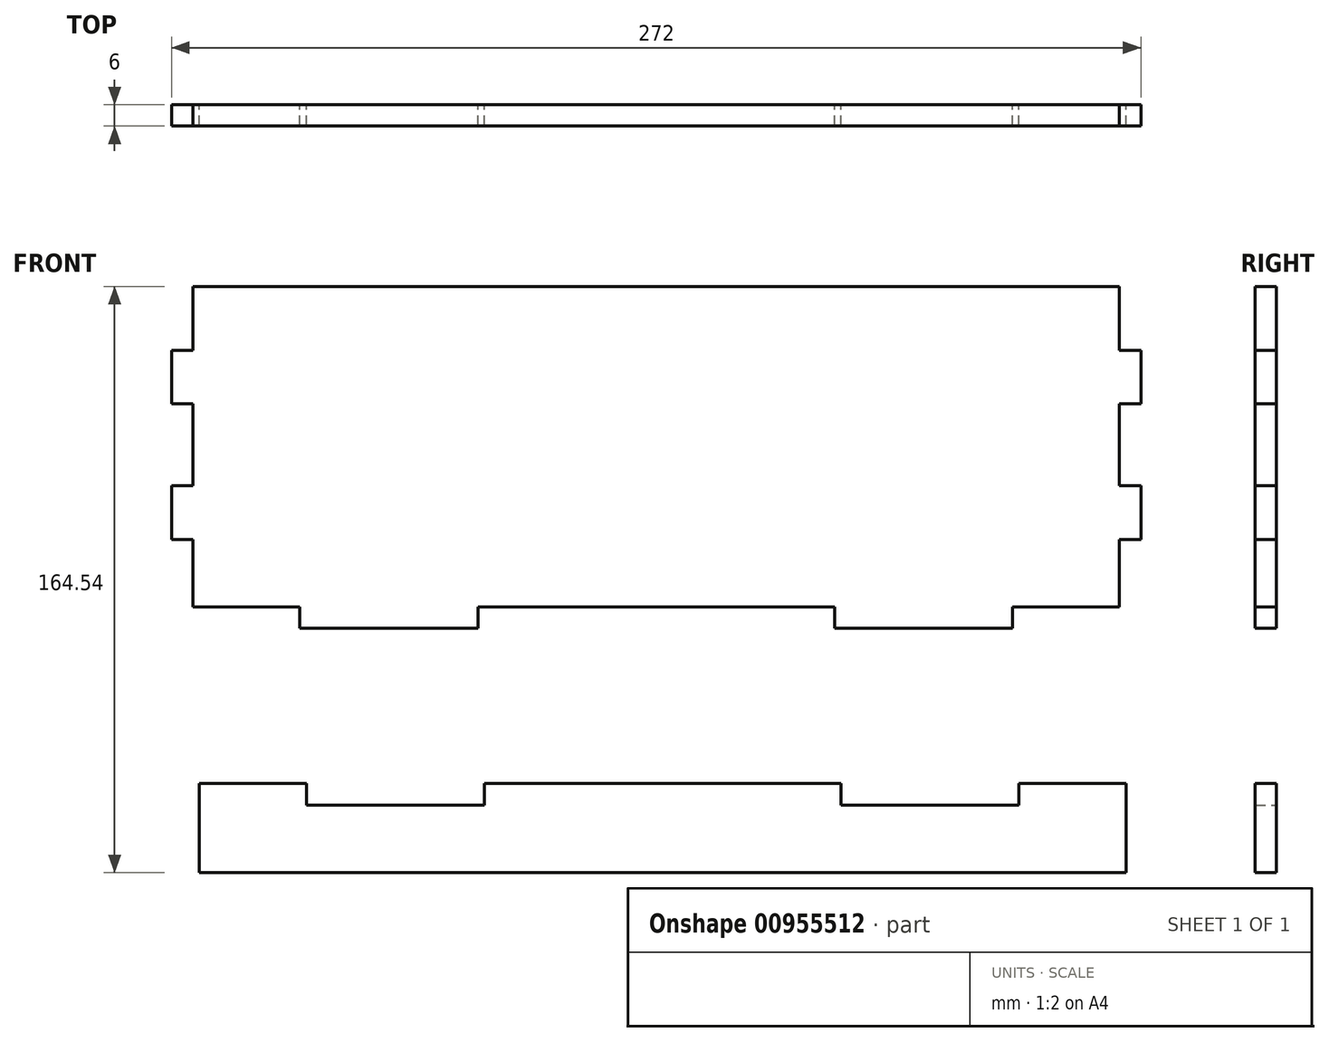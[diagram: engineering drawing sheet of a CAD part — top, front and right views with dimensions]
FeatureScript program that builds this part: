
annotation { "Feature Type Name" : "Feature", "Feature Type Description" : "" }
export const myFeature = defineFeature(function(context is Context, id is Id, definition is map)
    precondition{}
    {
        {
            var Q0;
            Q0=qCreatedBy(makeId("Front.planeOp"),FACE);
            var sketch = newSketch(context, id + "F0", { "sketchPlane" : qUnion([Q0])});
            skLineSegment(sketch, "E0.bottom", {"start": v(-45, 108.36) * mm, "end": v(215, 108.36) * mm});
            skLineSegment(sketch, "E0.top", {"start": v(-45, 18.36) * mm, "end": v(-15, 18.36) * mm});
            skLineSegment(sketch, "E0.left", {"start": v(-45, 108.36) * mm, "end": v(-45, 90.36) * mm});
            skLineSegment(sketch, "E0.right", {"start": v(215, 108.36) * mm, "end": v(215, 90.36) * mm});
            skLineSegment(sketch, "E1.bottom", {"start": v(-43.21, -31.18) * mm, "end": v(-13.21, -31.18) * mm});
            skLineSegment(sketch, "E1.top", {"start": v(-43.21, -56.18) * mm, "end": v(216.79, -56.18) * mm});
            skLineSegment(sketch, "E1.left", {"start": v(-43.21, -31.18) * mm, "end": v(-43.21, -56.18) * mm});
            skLineSegment(sketch, "E1.right", {"start": v(216.79, -31.18) * mm, "end": v(216.79, -56.18) * mm});
            skLineSegment(sketch, "E2.top", {"start": v(-15, 12.36) * mm, "end": v(35, 12.36) * mm});
            skLineSegment(sketch, "E2.left", {"start": v(-15, 18.36) * mm, "end": v(-15, 12.36) * mm});
            skLineSegment(sketch, "E2.right", {"start": v(35, 18.36) * mm, "end": v(35, 12.36) * mm});
            skLineSegment(sketch, "E3.top", {"start": v(135, 12.36) * mm, "end": v(185, 12.36) * mm});
            skLineSegment(sketch, "E3.left", {"start": v(135, 18.36) * mm, "end": v(135, 12.36) * mm});
            skLineSegment(sketch, "E3.right", {"start": v(185, 18.36) * mm, "end": v(185, 12.36) * mm});
            skLineSegment(sketch, "E4.top", {"start": v(-13.21, -37.18) * mm, "end": v(36.79, -37.18) * mm});
            skLineSegment(sketch, "E4.left", {"start": v(-13.21, -31.18) * mm, "end": v(-13.21, -37.18) * mm});
            skLineSegment(sketch, "E4.right", {"start": v(36.79, -31.18) * mm, "end": v(36.79, -37.18) * mm});
            skLineSegment(sketch, "E5.top", {"start": v(136.79, -37.18) * mm, "end": v(186.79, -37.18) * mm});
            skLineSegment(sketch, "E5.left", {"start": v(136.79, -31.18) * mm, "end": v(136.79, -37.18) * mm});
            skLineSegment(sketch, "E5.right", {"start": v(186.79, -31.18) * mm, "end": v(186.79, -37.18) * mm});
            skLineSegment(sketch, "E6.bottom", {"start": v(-45, 90.36) * mm, "end": v(-51, 90.36) * mm});
            skLineSegment(sketch, "E6.top", {"start": v(-45, 75.36) * mm, "end": v(-51, 75.36) * mm});
            skLineSegment(sketch, "E6.right", {"start": v(-51, 90.36) * mm, "end": v(-51, 75.36) * mm});
            skLineSegment(sketch, "E7.0.1.0", {"start": v(-45, 52.36) * mm, "end": v(-51, 52.36) * mm});
            skLineSegment(sketch, "E7.0.1.1", {"start": v(-51, 52.36) * mm, "end": v(-51, 37.36) * mm});
            skLineSegment(sketch, "E7.0.1.2", {"start": v(-45, 37.36) * mm, "end": v(-51, 37.36) * mm});
            skLineSegment(sketch, "E7.1.0.0", {"start": v(221, 90.36) * mm, "end": v(215, 90.36) * mm});
            skLineSegment(sketch, "E7.1.0.2", {"start": v(221, 75.36) * mm, "end": v(215, 75.36) * mm});
            skLineSegment(sketch, "E7.1.0.3", {"start": v(221, 90.36) * mm, "end": v(221, 75.36) * mm});
            skLineSegment(sketch, "E7.1.1.0", {"start": v(221, 52.36) * mm, "end": v(215, 52.36) * mm});
            skLineSegment(sketch, "E7.1.1.2", {"start": v(221, 37.36) * mm, "end": v(215, 37.36) * mm});
            skLineSegment(sketch, "E7.1.1.3", {"start": v(221, 52.36) * mm, "end": v(221, 37.36) * mm});
            skLineSegment(sketch, "E7.direction1", {"start": v(-51, 90.36) * mm, "end": v(215, 90.36) * mm, "construction": true});
            skLineSegment(sketch, "E7.direction2", {"start": v(-51, 90.36) * mm, "end": v(-51, 52.36) * mm, "construction": true});
            skLineSegment(sketch, "E8.trimOffspring", {"start": v(215, 37.36) * mm, "end": v(215, 18.36) * mm});
            skLineSegment(sketch, "E9.trimOffspring", {"start": v(215, 75.36) * mm, "end": v(215, 52.36) * mm});
            skLineSegment(sketch, "E10.trimOffspring", {"start": v(-45, 75.36) * mm, "end": v(-45, 52.36) * mm});
            skLineSegment(sketch, "E11.trimOffspring", {"start": v(-45, 37.36) * mm, "end": v(-45, 18.36) * mm});
            skLineSegment(sketch, "E12.trimOffspring", {"start": v(36.79, -31.18) * mm, "end": v(136.79, -31.18) * mm});
            skLineSegment(sketch, "E13.trimOffspring", {"start": v(186.79, -31.18) * mm, "end": v(216.79, -31.18) * mm});
            skLineSegment(sketch, "E14.trimOffspring", {"start": v(35, 18.36) * mm, "end": v(135, 18.36) * mm});
            skLineSegment(sketch, "E15.trimOffspring", {"start": v(185, 18.36) * mm, "end": v(215, 18.36) * mm});
            skSolve(sketch);
        }
        {
            var Q0;
            Q0=makeQuery(id+"F0.imprint","IMPRINT",FACE,{"disambiguationData":[TD([[makeQuery(id+"F0.imprint","IMPRINT",EDGE,{"derivedFrom":sQuery(id+"F0.wireOp",EDGE,"E0.bottom")}),-1.0]])]});
            var Q1;
            Q1=makeQuery(id+"F0.imprint","IMPRINT",FACE,{"disambiguationData":[TD([[makeQuery(id+"F0.imprint","IMPRINT",EDGE,{"derivedFrom":sQuery(id+"F0.wireOp",EDGE,"E1.bottom")}),-1.0]])]});
            extrude(context, id + "F1", {"entities" : qUnion([Q0, Q1]), "depth" : 6 * mm, "offsetDistance" : 25 * mm});
        }
    });
